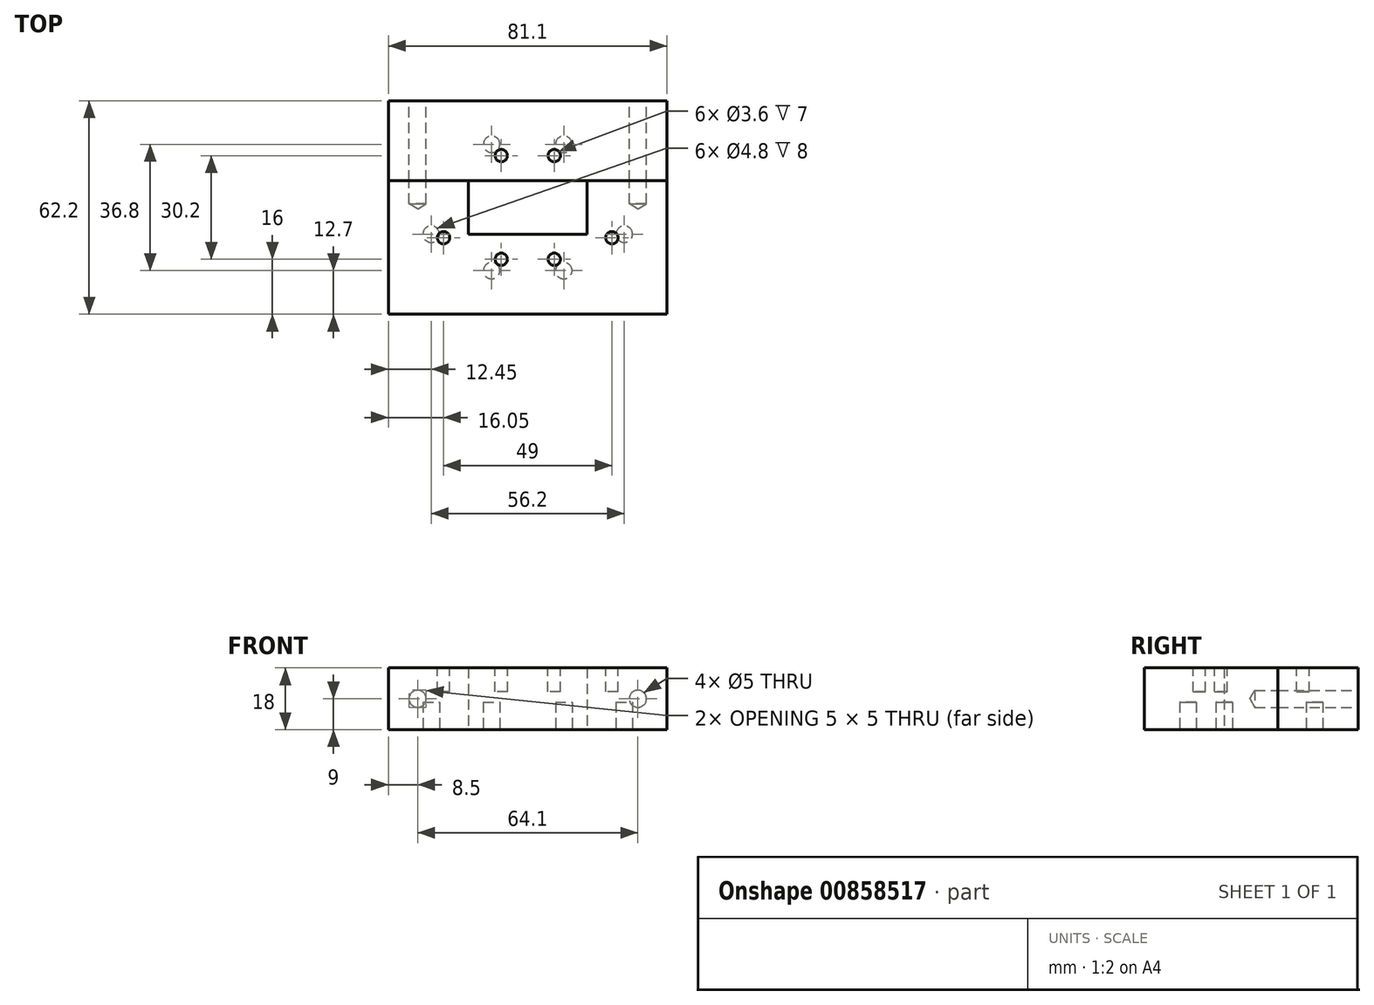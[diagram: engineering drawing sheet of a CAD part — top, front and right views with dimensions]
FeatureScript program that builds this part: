
annotation { "Feature Type Name" : "Feature", "Feature Type Description" : "" }
export const myFeature = defineFeature(function(context is Context, id is Id, definition is map)
    precondition{}
    {
        {
            var Q0;
            Q0=qCreatedBy(makeId("Top.planeOp"),FACE);
            var sketch = newSketch(context, id + "F0", { "sketchPlane" : qUnion([Q0])});
            skLineSegment(sketch, "E0.bottom", {"start": v(0, 0) * mm, "end": v(81.1, 0) * mm});
            skLineSegment(sketch, "E0.top", {"start": v(0, 62.2) * mm, "end": v(81.1, 62.2) * mm});
            skLineSegment(sketch, "E0.left", {"start": v(0, 0) * mm, "end": v(0, 62.2) * mm});
            skLineSegment(sketch, "E0.right", {"start": v(81.1, 0) * mm, "end": v(81.1, 62.2) * mm});
            skLineSegment(sketch, "E1.bottom", {"start": v(23.25, 23.3) * mm, "end": v(57.85, 23.3) * mm});
            skLineSegment(sketch, "E1.top", {"start": v(23.25, 38.9) * mm, "end": v(57.85, 38.9) * mm});
            skLineSegment(sketch, "E1.left", {"start": v(23.25, 23.3) * mm, "end": v(23.25, 38.9) * mm});
            skLineSegment(sketch, "E1.right", {"start": v(57.85, 23.3) * mm, "end": v(57.85, 38.9) * mm});
            skPoint(sketch, "E2", {"position": v(23.25, 31.1) * mm});
            skPoint(sketch, "E3", {"position": v(0, 31.1) * mm});
            skPoint(sketch, "E4", {"position": v(40.55, 62.2) * mm});
            skPoint(sketch, "E5", {"position": v(40.55, 38.9) * mm});
            skSolve(sketch);
        }
        {
            var Q0;
            Q0=makeQuery(id+"F0.imprint","IMPRINT",FACE,{"disambiguationData":[TD([[makeQuery(id+"F0.imprint","IMPRINT",EDGE,{"derivedFrom":sQuery(id+"F0.wireOp",EDGE,"E0.bottom")}),1.0]])]});
            extrude(context, id + "F1", {"entities" : qUnion([Q0]), "depth" : 18 * mm, "offsetDistance" : 25 * mm});
        }
        {
            var Q0;
            Q0=makeQuery(id+"F1.opExtrude","CAP_FACE",FACE,{"disambiguationData":[OSD([sQuery(id+"F0.wireOp",EDGE,"E0.bottom"),sQuery(id+"F0.wireOp",EDGE,"E0.top"),sQuery(id+"F0.wireOp",EDGE,"E0.left"),sQuery(id+"F0.wireOp",EDGE,"E0.right"),sQuery(id+"F0.wireOp",EDGE,"E1.bottom"),sQuery(id+"F0.wireOp",EDGE,"E1.top"),sQuery(id+"F0.wireOp",EDGE,"E1.left"),sQuery(id+"F0.wireOp",EDGE,"E1.right")])],"isStart":false});
            var sketch = newSketch(context, id + "F2", { "sketchPlane" : qUnion([Q0])});
            skCircle(sketch, "E6", {"center": v(32.85, 46.2) * mm, "radius": 1.8 * mm});
            skCircle(sketch, "E7", {"center": v(48.25, 46.2) * mm, "radius": 1.8 * mm});
            skCircle(sketch, "E8", {"center": v(65.05, 22.3) * mm, "radius": 1.8 * mm});
            skCircle(sketch, "E9", {"center": v(48.25, 16) * mm, "radius": 1.8 * mm});
            skCircle(sketch, "E10", {"center": v(32.85, 16) * mm, "radius": 1.8 * mm});
            skCircle(sketch, "E11", {"center": v(16.05, 22.3) * mm, "radius": 1.8 * mm});
            skLineSegment(sketch, "E12", {"start": v(57.85, 31.1) * mm, "end": v(23.25, 31.1) * mm, "construction": true});
            skLineSegment(sketch, "E13", {"start": v(40.55, 38.9) * mm, "end": v(40.55, 23.3) * mm, "construction": true});
            skSolve(sketch);
        }
        {
            var Q0;
            Q0 = qSketchRegion(id + "F2", true);
            extrude(context, id + "F3", {"entities" : qUnion([Q0]), "operationType" : NewBodyOperationType.REMOVE, "oppositeDirection" : true, "depth" : 7 * mm, "offsetDistance" : 25 * mm});
        }
        {
            var Q0;
            Q0=makeQuery(id+"F1.opExtrude","CAP_FACE",FACE,{"disambiguationData":[OSD([sQuery(id+"F0.wireOp",EDGE,"E0.bottom"),sQuery(id+"F0.wireOp",EDGE,"E0.top"),sQuery(id+"F0.wireOp",EDGE,"E0.left"),sQuery(id+"F0.wireOp",EDGE,"E0.right"),sQuery(id+"F0.wireOp",EDGE,"E1.bottom"),sQuery(id+"F0.wireOp",EDGE,"E1.top"),sQuery(id+"F0.wireOp",EDGE,"E1.left"),sQuery(id+"F0.wireOp",EDGE,"E1.right")])],"isStart":true});
            var sketch = newSketch(context, id + "F4", { "sketchPlane" : qUnion([Q0])});
            skCircle(sketch, "E14", {"center": v(51.05, -49.5) * mm, "radius": 2.4 * mm});
            skCircle(sketch, "E15", {"center": v(30.05, -49.5) * mm, "radius": 2.4 * mm});
            skCircle(sketch, "E16", {"center": v(12.45, -23.3) * mm, "radius": 2.4 * mm});
            skCircle(sketch, "E17", {"center": v(30.05, -12.7) * mm, "radius": 2.4 * mm});
            skCircle(sketch, "E18", {"center": v(51.05, -12.7) * mm, "radius": 2.4 * mm});
            skCircle(sketch, "E19", {"center": v(68.65, -23.3) * mm, "radius": 2.4 * mm});
            skLineSegment(sketch, "E20", {"start": v(40.55, -38.9) * mm, "end": v(40.55, -23.3) * mm, "construction": true});
            skLineSegment(sketch, "E21", {"start": v(23.25, -31.1) * mm, "end": v(57.85, -31.1) * mm, "construction": true});
            skSolve(sketch);
        }
        {
            var Q0;
            Q0 = qSketchRegion(id + "F4", true);
            extrude(context, id + "F5", {"entities" : qUnion([Q0]), "operationType" : NewBodyOperationType.REMOVE, "oppositeDirection" : true, "depth" : 8 * mm, "offsetDistance" : 25 * mm});
        }
        {
            var Q0;
            Q0=makeQuery(id+"F1.opExtrude","CAP_FACE",FACE,{"disambiguationData":[OSD([sQuery(id+"F0.wireOp",EDGE,"E0.bottom"),sQuery(id+"F0.wireOp",EDGE,"E0.top"),sQuery(id+"F0.wireOp",EDGE,"E0.left"),sQuery(id+"F0.wireOp",EDGE,"E0.right"),sQuery(id+"F0.wireOp",EDGE,"E1.bottom"),sQuery(id+"F0.wireOp",EDGE,"E1.top"),sQuery(id+"F0.wireOp",EDGE,"E1.left"),sQuery(id+"F0.wireOp",EDGE,"E1.right")])],"isStart":false});
            var sketch = newSketch(context, id + "F6", { "sketchPlane" : qUnion([Q0])});
            skLineSegment(sketch, "E22.bottom", {"start": v(0, 38.9) * mm, "end": v(81.1, 38.9) * mm});
            skLineSegment(sketch, "E22.top", {"start": v(0, 38.93) * mm, "end": v(81.1, 38.93) * mm});
            skLineSegment(sketch, "E22.left", {"start": v(0, 38.9) * mm, "end": v(0, 38.93) * mm});
            skLineSegment(sketch, "E22.right", {"start": v(81.1, 38.9) * mm, "end": v(81.1, 38.93) * mm});
            skSolve(sketch);
        }
        {
            var Q0;
            Q0 = qSketchRegion(id + "F6", true);
            extrude(context, id + "F7", {"entities" : qUnion([Q0]), "operationType" : NewBodyOperationType.REMOVE, "endBound" : BoundingType.THROUGH_ALL, "oppositeDirection" : true, "depth" : 25 * mm, "offsetDistance" : 25 * mm});
        }
        {
            var Q0;
            Q0=makeQuery(id+"F1.opExtrude","SWEPT_FACE",FACE,{"disambiguationData":[OSD([sQuery(id+"F0.wireOp",EDGE,"E0.top")])]});
            var sketch = newSketch(context, id + "F8", { "sketchPlane" : qUnion([Q0])});
            skPoint(sketch, "E23", {"position": v(-72.6, 9) * mm});
            skPoint(sketch, "E24", {"position": v(-8.5, 9) * mm});
            skLineSegment(sketch, "E25", {"start": v(-40.55, 18) * mm, "end": v(-40.55, 0) * mm, "construction": true});
            skSolve(sketch);
        }
        {
            var Q0;
            Q0=sQuery(id+"F8.wireOp",VERTEX,"E24");
            var Q1;
            Q1=sQuery(id+"F8.wireOp",VERTEX,"E23");
            var Q2;
            Q2=makeQuery(id+"F7.boolean.opBoolean","SPLIT",BODY,{"disambiguationData":[OD(0.0)],"derivedFrom":makeQuery(id+"F1.opExtrude","SWEPT_BODY",BODY,{"disambiguationData":[OSD([sQuery(id+"F0.wireOp",EDGE,"E0.bottom"),sQuery(id+"F0.wireOp",EDGE,"E0.top"),sQuery(id+"F0.wireOp",EDGE,"E0.left"),sQuery(id+"F0.wireOp",EDGE,"E0.right"),sQuery(id+"F0.wireOp",EDGE,"E1.bottom"),sQuery(id+"F0.wireOp",EDGE,"E1.top"),sQuery(id+"F0.wireOp",EDGE,"E1.left"),sQuery(id+"F0.wireOp",EDGE,"E1.right")])]})});
            var Q3;
            Q3=makeQuery(id+"F7.boolean.opBoolean","SPLIT",BODY,{"disambiguationData":[OD(1.0)],"derivedFrom":makeQuery(id+"F1.opExtrude","SWEPT_BODY",BODY,{"disambiguationData":[OSD([sQuery(id+"F0.wireOp",EDGE,"E0.bottom"),sQuery(id+"F0.wireOp",EDGE,"E0.top"),sQuery(id+"F0.wireOp",EDGE,"E0.left"),sQuery(id+"F0.wireOp",EDGE,"E0.right"),sQuery(id+"F0.wireOp",EDGE,"E1.bottom"),sQuery(id+"F0.wireOp",EDGE,"E1.top"),sQuery(id+"F0.wireOp",EDGE,"E1.left"),sQuery(id+"F0.wireOp",EDGE,"E1.right")])]})});
            hole(context, id + "F9", {"style" : HoleStyle.SIMPLE, "endStyle" : HoleEndStyle.BLIND, "standardTappedOrClearance" : lookupTablePath({ "standard" : "ISO", "engagement" : "75%", "pitch" : "1 mm", "size" : "M6", "type" : "Tapped" }), "standardBlindInLast" : lookupTablePath({ "standard" : "ISO", "engagement" : "75%", "pitch" : "1 mm", "size" : "M6", "type" : "Tapped" }), "holeDiameter" : 5 * mm, "majorDiameter" : 6 * mm, "showTappedDepth" : true, "holeDepth" : 30 * mm, "isTappedThrough" : true, "tappedDepth" : 27 * mm, "tapClearance" : 3, "locations" : qUnion([Q0, Q1]), "scope" : qUnion([Q2, Q3])});
        }
    });
